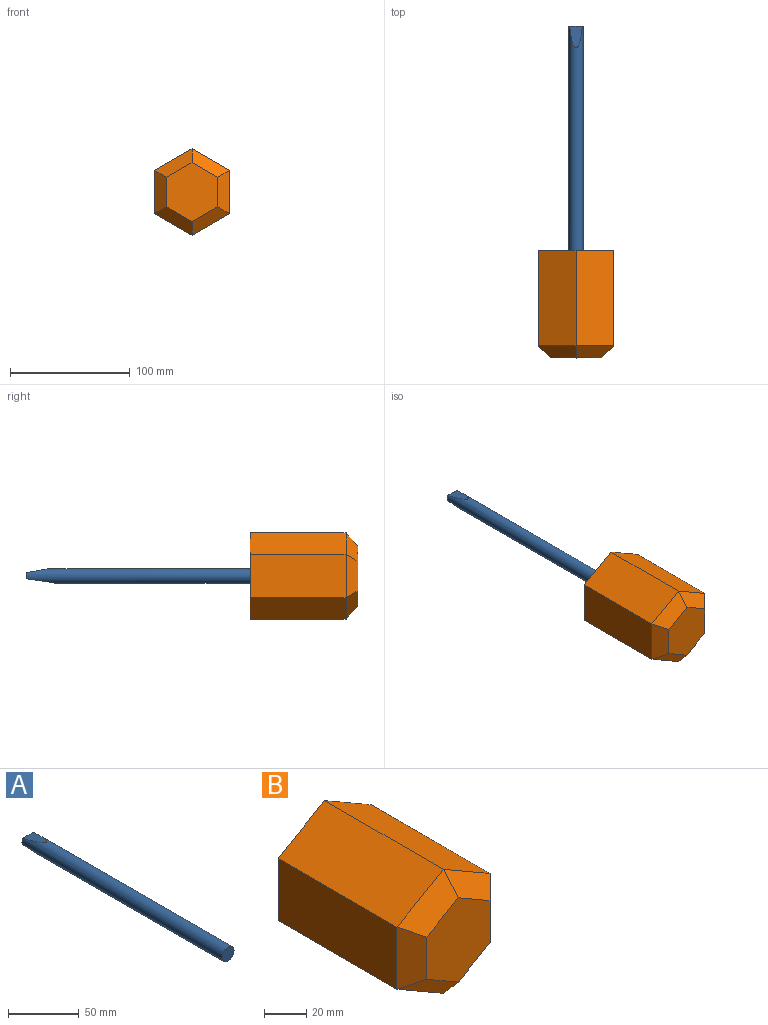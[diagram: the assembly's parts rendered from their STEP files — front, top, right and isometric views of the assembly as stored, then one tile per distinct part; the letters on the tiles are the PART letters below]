
ASSEMBLY  parts=2 mates=1
PART A: 7 faces, bbox 12x200x12 mm
  f0: cylinder r=6mm len=200mm, axis (0,1,0), area 7146.2mm2, adj f1,f2,f3,f4,f5,f6
  f1: plane 12x5.05mm, normal (0,1,0), area 58.7mm2, adj f0,f3,f4
  f2: plane 12x12mm, normal (0,-1,0), area 113.1mm2, adj f0
  f3: plane 21.4x11.12mm, normal (0,0.14,-0.99), area 195.3mm2, adj f0,f1,f5
  f4: plane 18.35x10.63mm, normal (0,0.17,0.99), area 141.1mm2, adj f0,f1
  f5: plane 5.73x0.19mm, normal (0,-0.09,-1), area 1.1mm2, adj f0,f3,f6
  f6: plane 5.73x2.91mm, normal (0,0.24,-0.97), area 11.6mm2, adj f0,f5
PART B: 16 faces, bbox 62.5x90x72.2 mm
  f0: plane 80x31.27mm, normal (0.5,0,-0.87), area 2888.5mm2, adj f1,f5,f7,f13
  f1: plane 80x36.11mm, normal (1,0,0), area 2888.5mm2, adj f0,f2,f7,f12
  f2: plane 80x31.27mm, normal (0.5,0,0.87), area 2888.5mm2, adj f1,f3,f7,f10
  f3: plane 80x31.27mm, normal (-0.5,0,0.87), area 2888.5mm2, adj f2,f4,f7,f8
  f4: plane 80x36.11mm, normal (-1,0,0), area 2888.5mm2, adj f3,f5,f7,f9
  f5: plane 80x31.27mm, normal (-0.5,0,-0.87), area 2888.5mm2, adj f0,f4,f7,f11
  f6: plane 49.12x42.54mm, normal (0,-1,0), area 1567mm2, adj f8,f9,f10,f11,f12,f13
  f7: plane 72.21x62.54mm, normal (0,1,0), area 3273.9mm2, adj f0,f1,f2,f3,f4,f5,f14
  f8: plane 31.27x23.83mm, normal (-0.35,-0.71,0.61), area 429mm2, adj f3,f6,f9,f10
  f9: plane 36.11x10mm, normal (-0.71,-0.71,0), area 429mm2, adj f4,f6,f8,f11
  f10: plane 31.27x23.83mm, normal (0.35,-0.71,0.61), area 429mm2, adj f2,f6,f8,f12
  f11: plane 31.27x23.83mm, normal (-0.35,-0.71,-0.61), area 429mm2, adj f5,f6,f9,f13
  f12: plane 36.11x10mm, normal (0.71,-0.71,0), area 429mm2, adj f1,f6,f10,f13
  f13: plane 31.27x23.83mm, normal (0.35,-0.71,-0.61), area 429mm2, adj f0,f6,f11,f12
  f14: cylinder r=6mm len=12.5mm, axis (0,1,0), area 471.2mm2, adj f7,f15
  f15: plane 12x12mm, normal (0,1,0), area 113.1mm2, adj f14
PLACE A t=(0.27,209.42,-0.22)mm
PLACE B t=(0.27,21.92,-0.22)mm
MATE fastened A.f0 <-> B.f14  axis (0,1,0) through (0.27,9.42,-0.22)mm
